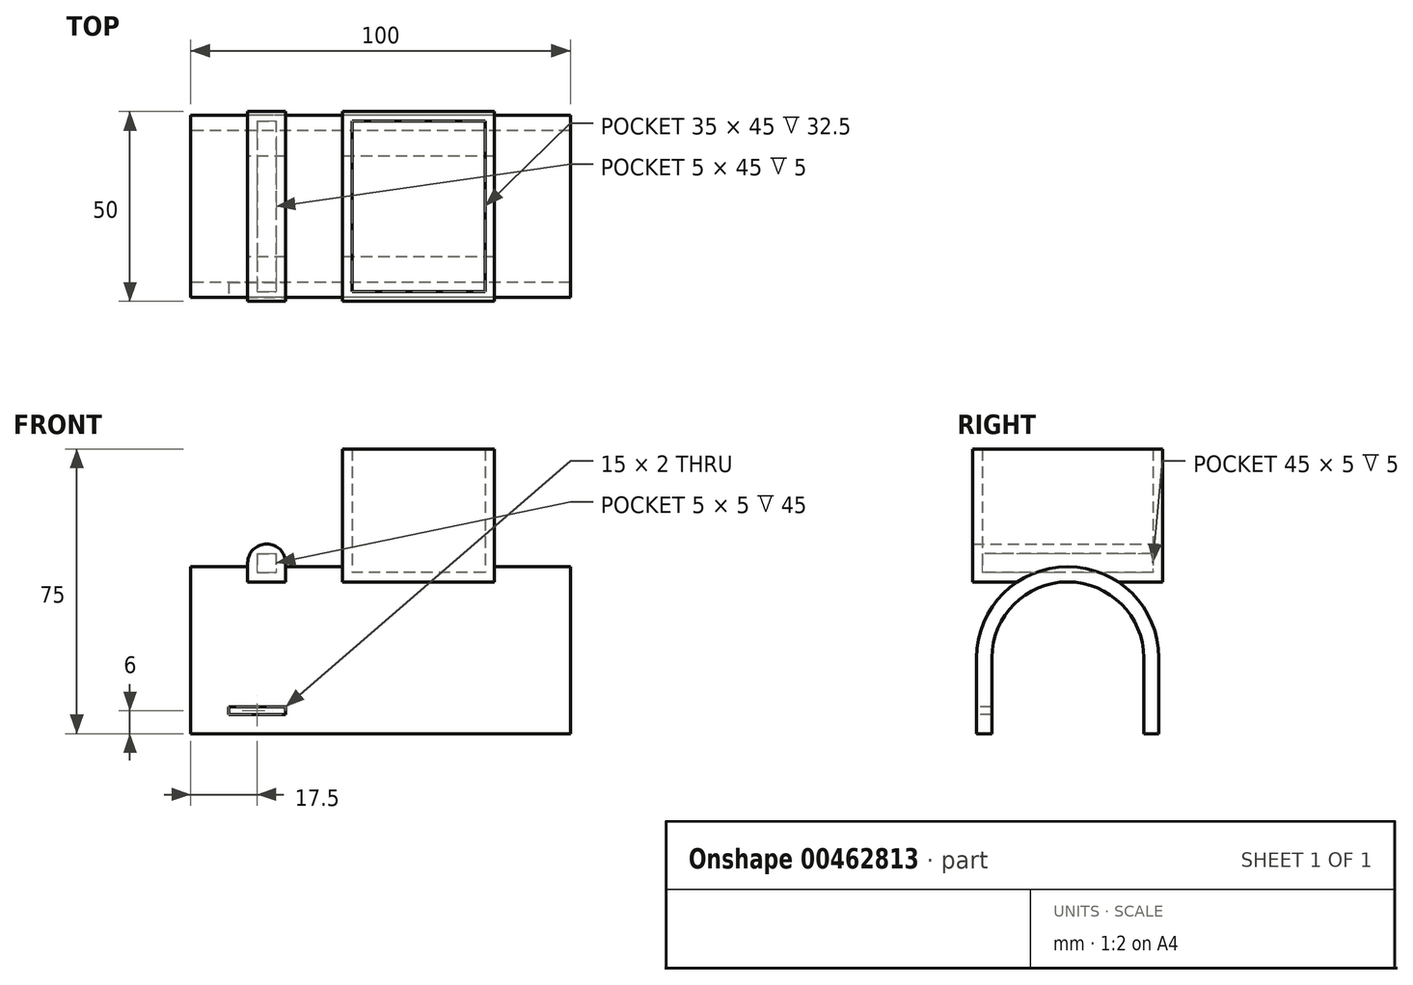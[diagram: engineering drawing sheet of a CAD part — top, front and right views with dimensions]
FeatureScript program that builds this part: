
annotation { "Feature Type Name" : "Feature", "Feature Type Description" : "" }
export const myFeature = defineFeature(function(context is Context, id is Id, definition is map)
    precondition{}
    {
        {
            var Q0;
            Q0=qCreatedBy(makeId("Right.planeOp"),FACE);
            var sketch = newSketch(context, id + "F0", { "sketchPlane" : qUnion([Q0])});
            skLineSegment(sketch, "E0.bottom", {"start": v(-20, 0) * mm, "end": v(-24, 0) * mm});
            skLineSegment(sketch, "E0.top", {"start": v(-20, 20) * mm, "end": v(-24, 20) * mm});
            skLineSegment(sketch, "E0.left", {"start": v(-20, 0) * mm, "end": v(-20, 20) * mm});
            skLineSegment(sketch, "E0.right", {"start": v(-24, 0) * mm, "end": v(-24, 20) * mm});
            skLineSegment(sketch, "E1.MirrorCS", {"start": v(20, 0) * mm, "end": v(24, 0) * mm});
            skLineSegment(sketch, "E2.MirrorCS", {"start": v(20, 20) * mm, "end": v(24, 20) * mm});
            skLineSegment(sketch, "E3.MirrorCS", {"start": v(24, 0) * mm, "end": v(24, 20) * mm});
            skLineSegment(sketch, "E4.MirrorCS", {"start": v(20, 0) * mm, "end": v(20, 20) * mm});
            skArc(sketch, "E5", {"start": v(20, 20) * mm, "mid": v(0, 40) * mm, "end": v(-20, 20) * mm});
            skArc(sketch, "E6", {"start": v(24, 20) * mm, "mid": v(0, 44) * mm, "end": v(-24, 20) * mm});
            skSolve(sketch);
        }
        {
            var Q0;
            Q0=qCreatedBy(makeId("Top.planeOp"),FACE);
            cPlane(context, id + "F1", {"entities" : qUnion([Q0]), "cplaneType" : CPlaneType.OFFSET, "offset" : 40 * mm, "width" : 150 * mm, "height" : 150 * mm});
        }
        {
            var Q0;
            Q0 = qSketchRegion(id + "F0", true);
            extrude(context, id + "F2", {"entities" : qUnion([Q0]), "depth" : 100 * mm});
        }
        {
            var Q0;
            Q0=qCreatedBy(id+"F1.planeOp",FACE);
            var sketch = newSketch(context, id + "F3", { "sketchPlane" : qUnion([Q0])});
            skLineSegment(sketch, "E7.bottom", {"start": v(15, 25) * mm, "end": v(25, 25) * mm});
            skLineSegment(sketch, "E7.top", {"start": v(15, -25) * mm, "end": v(25, -25) * mm});
            skLineSegment(sketch, "E7.left", {"start": v(15, 25) * mm, "end": v(15, -25) * mm});
            skLineSegment(sketch, "E7.right", {"start": v(25, 25) * mm, "end": v(25, -25) * mm});
            skLineSegment(sketch, "E8.bottom", {"start": v(80, 25) * mm, "end": v(40, 25) * mm});
            skLineSegment(sketch, "E8.top", {"start": v(80, -25) * mm, "end": v(40, -25) * mm});
            skLineSegment(sketch, "E8.left", {"start": v(80, 25) * mm, "end": v(80, -25) * mm});
            skLineSegment(sketch, "E8.right", {"start": v(40, 25) * mm, "end": v(40, -25) * mm});
            skSolve(sketch);
        }
        {
            var Q0;
            Q0 = qSketchRegion(id + "F3", true);
            extrude(context, id + "F4", {"entities" : qUnion([Q0]), "operationType" : NewBodyOperationType.ADD, "depth" : 10 * mm});
        }
        {
            var Q0;
            Q0=makeQuery(id+"F4.opExtrude","CAP_FACE",FACE,{"disambiguationData":[OSD([sQuery(id+"F3.wireOp",EDGE,"E8.bottom"),sQuery(id+"F3.wireOp",EDGE,"E8.top"),sQuery(id+"F3.wireOp",EDGE,"E8.left"),sQuery(id+"F3.wireOp",EDGE,"E8.right")])],"isStart":false});
            extrude(context, id + "F5", {"entities" : qUnion([Q0]), "operationType" : NewBodyOperationType.ADD, "depth" : 25 * mm});
        }
        {
            var Q0;
            Q0=makeQuery(id+"F5.opExtrude","CAP_FACE",FACE,{"disambiguationData":[OSD([sQuery(id+"F3.wireOp",EDGE,"E8.bottom"),sQuery(id+"F3.wireOp",EDGE,"E8.top"),sQuery(id+"F3.wireOp",EDGE,"E8.left"),sQuery(id+"F3.wireOp",EDGE,"E8.right")])],"isStart":false});
            shell(context, id + "F6", {"entities" : qUnion([Q0]), "thickness" : 2.5 * mm});
        }
        {
            var Q0;
            Q0=makeQuery(id+"F4.opExtrude","CAP_EDGE",EDGE,{"disambiguationData":[OSD([sQuery(id+"F3.wireOp",EDGE,"E7.left")])],"isStart":false});
            fillet(context, id + "F7", {"entities" : qUnion([Q0]), "radius" : 5 * mm, "tangentPropagation" : true, "allowEdgeOverflow" : false});
        }
        {
            var Q0;
            Q0=makeQuery(id+"F4.opExtrude","CAP_EDGE",EDGE,{"disambiguationData":[OSD([sQuery(id+"F3.wireOp",EDGE,"E7.right")])],"isStart":false});
            fillet(context, id + "F8", {"entities" : qUnion([Q0]), "radius" : 5 * mm, "tangentPropagation" : true, "allowEdgeOverflow" : false});
        }
        {
            var Q0;
            Q0=makeQuery(id+"F2.opExtrude","SWEPT_FACE",FACE,{"disambiguationData":[OSD([sQuery(id+"F0.wireOp",EDGE,"E0.right")])]});
            var sketch = newSketch(context, id + "F9", { "sketchPlane" : qUnion([Q0])});
            skLineSegment(sketch, "E9.bottom", {"start": v(10, 7) * mm, "end": v(25, 7) * mm});
            skLineSegment(sketch, "E9.top", {"start": v(10, 5) * mm, "end": v(25, 5) * mm});
            skLineSegment(sketch, "E9.left", {"start": v(10, 7) * mm, "end": v(10, 5) * mm});
            skLineSegment(sketch, "E9.right", {"start": v(25, 7) * mm, "end": v(25, 5) * mm});
            skSolve(sketch);
        }
        {
            var Q0;
            Q0=makeQuery(id+"F9.imprint","IMPRINT",FACE,{"disambiguationData":[TD([[makeQuery(id+"F9.imprint","IMPRINT",EDGE,{"derivedFrom":sQuery(id+"F9.wireOp",EDGE,"E9.bottom")}),-1.0]])]});
            extrude(context, id + "F10", {"entities" : qUnion([Q0]), "operationType" : NewBodyOperationType.REMOVE, "oppositeDirection" : true, "depth" : 25 * mm});
        }
    });
